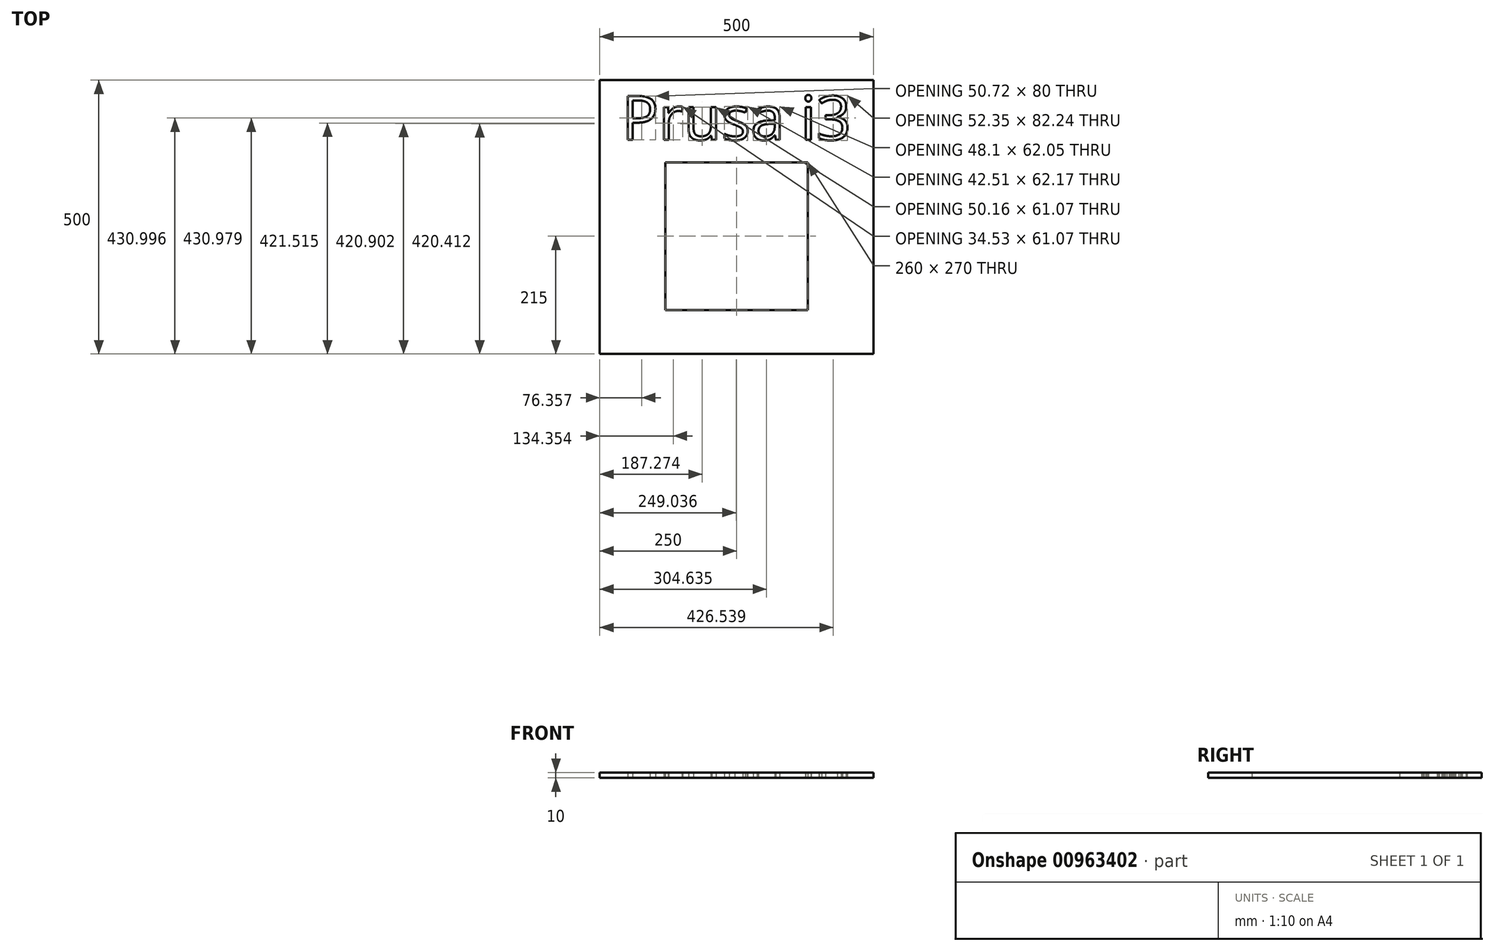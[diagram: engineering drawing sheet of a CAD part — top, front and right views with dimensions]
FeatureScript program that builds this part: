
annotation { "Feature Type Name" : "Feature", "Feature Type Description" : "" }
export const myFeature = defineFeature(function(context is Context, id is Id, definition is map)
    precondition{}
    {
        {
            var Q0;
            Q0=qCreatedBy(makeId("Top.planeOp"),FACE);
            var sketch = newSketch(context, id + "F0", { "sketchPlane" : qUnion([Q0])});
            skLineSegment(sketch, "E0.bottom", {"start": v(250, -250) * mm, "end": v(-250, -250) * mm});
            skLineSegment(sketch, "E0.top", {"start": v(250, 250) * mm, "end": v(-250, 250) * mm});
            skLineSegment(sketch, "E0.left", {"start": v(250, -250) * mm, "end": v(250, 250) * mm});
            skLineSegment(sketch, "E0.right", {"start": v(-250, -250) * mm, "end": v(-250, 250) * mm});
            skPoint(sketch, "E0.middle", {"position": v(0, 0) * mm});
            skLineSegment(sketch, "E1.bottom", {"start": v(-130, 100) * mm, "end": v(130, 100) * mm});
            skLineSegment(sketch, "E1.top", {"start": v(-130, -170) * mm, "end": v(130, -170) * mm});
            skLineSegment(sketch, "E1.left", {"start": v(-130, 100) * mm, "end": v(-130, -170) * mm});
            skLineSegment(sketch, "E1.right", {"start": v(130, 100) * mm, "end": v(130, -170) * mm});
            skText(sketch, "E2", { "text": "Prusa i3", "fontName": "OpenSans-Regular.ttf"});
            const initialGuessF0  = {"E2": [-0.21, 0.14098, 1, 0, 0.08068]};
            skSetInitialGuess(sketch, initialGuessF0);
            skSolve(sketch);
        }
        {
            var Q0;
            Q0=makeQuery(id+"F0.imprint","IMPRINT",FACE,{"disambiguationData":[TD([[makeQuery(id+"F0.imprint","IMPRINT",EDGE,{"derivedFrom":sQuery(id+"F0.wireOp",EDGE,"E0.bottom")}),-1.0]])]});
            extrude(context, id + "F1", {"entities" : qUnion([Q0]), "depth" : 10 * mm, "offsetDistance" : 25 * mm});
        }
        {
            var Q0;
            Q0=makeQuery(id+"F0.imprint","IMPRINT",FACE,{"disambiguationData":[TD([[makeQuery(id+"F0.imprint","IMPRINT",EDGE,{"derivedFrom":sQuery(id+"F0.wireOp",EDGE,"E2.sketch_text.stroke-8")}),1.0]])]});
            extrude(context, id + "F2", {"entities" : qUnion([Q0]), "depth" : 10 * mm, "offsetDistance" : 25 * mm});
        }
        {
            var Q0;
            Q0=makeQuery(id+"F0.imprint","IMPRINT",FACE,{"disambiguationData":[TD([[makeQuery(id+"F0.imprint","IMPRINT",EDGE,{"derivedFrom":sQuery(id+"F0.wireOp",EDGE,"E2.sketch_text.stroke-89")}),1.0]])]});
            extrude(context, id + "F3", {"entities" : qUnion([Q0]), "depth" : 10 * mm, "offsetDistance" : 25 * mm});
        }
    });
